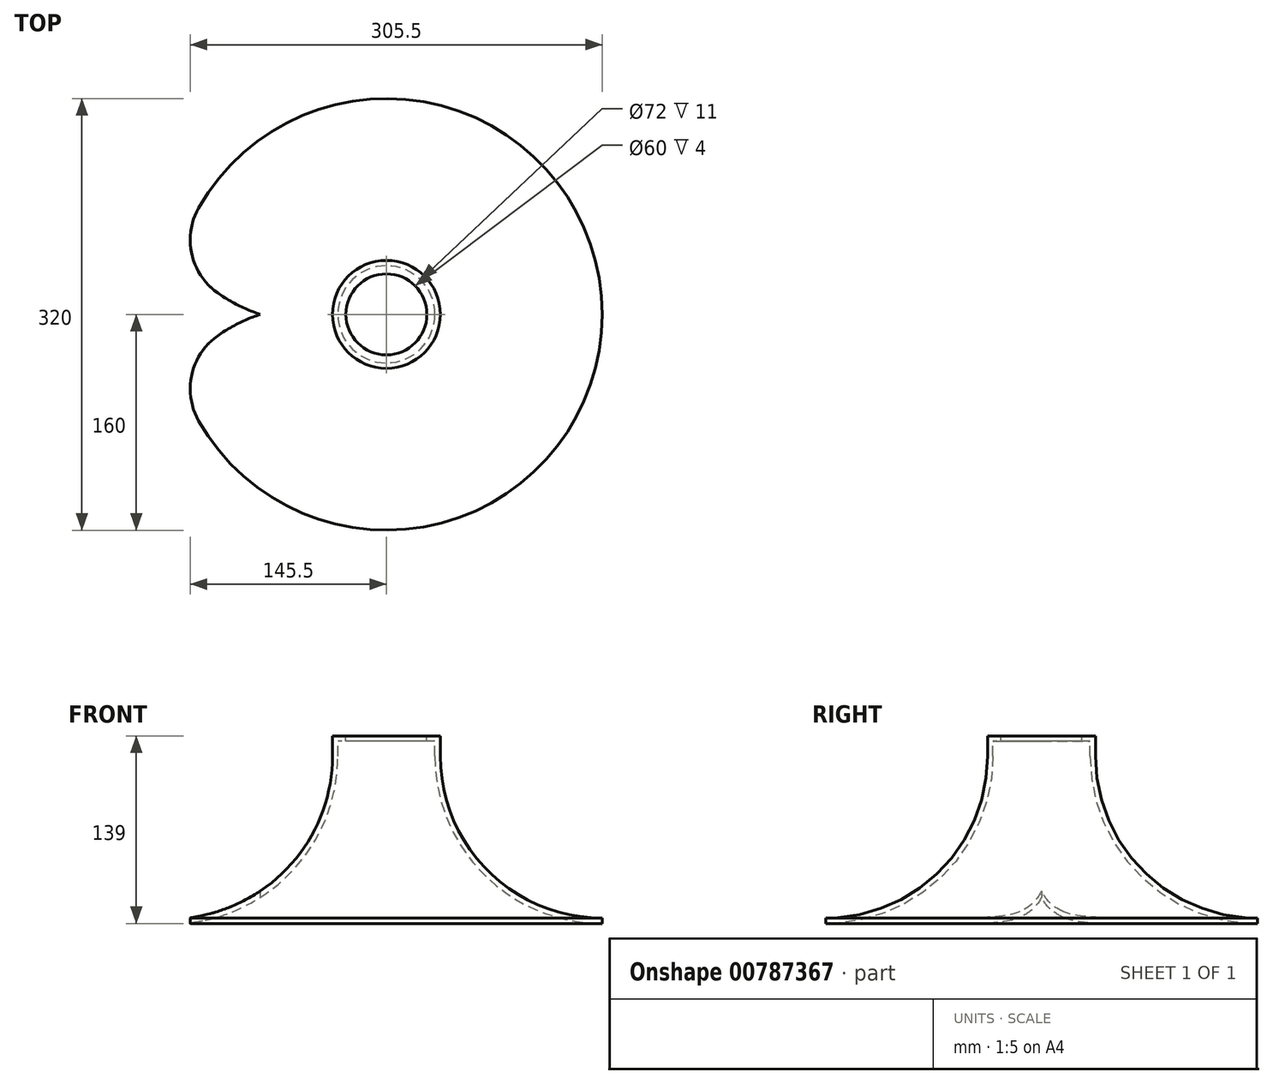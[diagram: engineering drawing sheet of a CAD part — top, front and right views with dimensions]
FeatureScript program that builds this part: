
annotation { "Feature Type Name" : "Feature", "Feature Type Description" : "" }
export const myFeature = defineFeature(function(context is Context, id is Id, definition is map)
    precondition{}
    {
        {
            var Q0;
            Q0=qCreatedBy(makeId("Front.planeOp"),FACE);
            var sketch = newSketch(context, id + "F0", { "sketchPlane" : qUnion([Q0])});
            skArc(sketch, "E0", {"start": v(0, -120) * mm, "mid": v(84.85, -84.85) * mm, "end": v(120, 0) * mm});
            skArc(sketch, "E1", {"start": v(0, -124) * mm, "mid": v(87.68, -87.68) * mm, "end": v(124, 0) * mm});
            skLineSegment(sketch, "E2", {"start": v(0, -124) * mm, "end": v(0, -120) * mm});
            skLineSegment(sketch, "E3.top", {"start": v(120, 15) * mm, "end": v(124, 15) * mm});
            skLineSegment(sketch, "E3.left", {"start": v(120, 0) * mm, "end": v(120, 15) * mm});
            skLineSegment(sketch, "E4.bottom", {"start": v(124, 15) * mm, "end": v(130, 15) * mm});
            skLineSegment(sketch, "E4.top", {"start": v(124, 11) * mm, "end": v(130, 11) * mm});
            skLineSegment(sketch, "E4.right", {"start": v(130, 15) * mm, "end": v(130, 11) * mm});
            skLineSegment(sketch, "E5", {"start": v(124, 11) * mm, "end": v(124, 0) * mm});
            skLineSegment(sketch, "E6", {"start": v(160, 28.66) * mm, "end": v(160, -153.48) * mm, "construction": true});
            skSolve(sketch);
        }
        {
            var Q0;
            Q0=makeQuery(id+"F0.imprint","IMPRINT",FACE,{"disambiguationData":[TD([[makeQuery(id+"F0.imprint","IMPRINT",EDGE,{"derivedFrom":sQuery(id+"F0.wireOp",EDGE,"E0")}),-1.0]])]});
            var Q1;
            Q1=sQuery(id+"F0.wireOp",EDGE,"E6");
            revolve(context, id + "F1", {"surfaceOperationType" : NewSurfaceOperationType.NEW, "entities" : qUnion([Q0]), "axis" : qUnion([Q1]), "revolveType" : RevolveType.FULL});
        }
        {
            var Q0;
            Q0=qCreatedBy(makeId("Top.planeOp"),FACE);
            cPlane(context, id + "F2", {"entities" : qUnion([Q0]), "cplaneType" : CPlaneType.OFFSET, "offset" : 140 * mm, "oppositeDirection" : true, "width" : 150 * mm, "height" : 150 * mm});
        }
        {
            var Q0;
            Q0=qCreatedBy(id+"F2.planeOp",FACE);
            var sketch = newSketch(context, id + "F3", { "sketchPlane" : qUnion([Q0])});
            skArc(sketch, "E7", {"start": v(0, 54.14) * mm, "mid": v(28.25, 20.93) * mm, "end": v(66.5, 0) * mm});
            skLineSegment(sketch, "E8", {"start": v(0, 54.14) * mm, "end": v(0, 0) * mm});
            skLineSegment(sketch, "E9", {"start": v(0, 0) * mm, "end": v(0, -54.14) * mm});
            skArc(sketch, "E10", {"start": v(66.5, 0) * mm, "mid": v(28.25, -20.93) * mm, "end": v(0, -54.14) * mm});
            skSolve(sketch);
        }
        {
            var Q0;
            Q0=makeQuery(id+"F3.imprint","IMPRINT",FACE,{"disambiguationData":[TD([[makeQuery(id+"F3.imprint","IMPRINT",EDGE,{"derivedFrom":sQuery(id+"F3.wireOp",EDGE,"E7")}),-1.0]])]});
            extrude(context, id + "F4", {"entities" : qUnion([Q0]), "operationType" : NewBodyOperationType.REMOVE, "depth" : 67 * mm, "offsetDistance" : 25 * mm});
        }
        {
            var Q0;
            Q0=makeQuery(id+"F4.boolean.opBoolean","INTERSECT",EDGE,{"derivedFrom":[makeQuery(id+"F1.opRevolve","SWEPT_FACE",FACE,{"disambiguationData":[OSD([sQuery(id+"F0.wireOp",EDGE,"E2")])]}),makeQuery(id+"F4.opExtrude","SWEPT_FACE",FACE,{"disambiguationData":[OSD([sQuery(id+"F3.wireOp",EDGE,"E10")])]})]});
            var Q1;
            Q1=makeQuery(id+"F4.boolean.opBoolean","INTERSECT",EDGE,{"derivedFrom":[makeQuery(id+"F1.opRevolve","SWEPT_FACE",FACE,{"disambiguationData":[OSD([sQuery(id+"F0.wireOp",EDGE,"E2")])]}),makeQuery(id+"F4.opExtrude","SWEPT_FACE",FACE,{"disambiguationData":[OSD([sQuery(id+"F3.wireOp",EDGE,"E7")])]})]});
            var Q2;
            {var subQ0=sQuery(id+"F3.wireOp",EDGE,"E10");var subQ2=makeQuery(id+"F4.boolean.opBoolean","COPY",FACE,{"derivedFrom":makeQuery(id+"F4.opExtrude","SWEPT_FACE",FACE,{"disambiguationData":[OSD([sQuery(id+"F3.wireOp",EDGE,"E7")])]})});Q2=makeQuery(id+"Fn1Wq9QeC9tYu7w_1.5.F4.boolean.opBoolean","INTERSECT",EDGE,{"derivedFrom":[makeQuery(id+"Fn1Wq9QeC9tYu7w_1.4.F4.boolean.opBoolean","SPLIT",FACE,{"disambiguationData":[TD([subQ2])],"derivedFrom":makeQuery(id+"Fn1Wq9QeC9tYu7w_1.3.F4.boolean.opBoolean","SPLIT",FACE,{"disambiguationData":[TD([subQ2])],"derivedFrom":makeQuery(id+"Fn1Wq9QeC9tYu7w_1.2.F4.boolean.opBoolean","SPLIT",FACE,{"disambiguationData":[TD([subQ2])],"derivedFrom":makeQuery(id+"Fn1Wq9QeC9tYu7w_1.1.F4.boolean.opBoolean","SPLIT",FACE,{"disambiguationData":[TD([subQ2])],"derivedFrom":makeQuery(id+"F1.opRevolve","SWEPT_FACE",FACE,{"disambiguationData":[OSD([sQuery(id+"F0.wireOp",EDGE,"E2")])]})})})})}),makeQuery(id+"Fn1Wq9QeC9tYu7w_1.5.F4.opExtrude","SWEPT_FACE",FACE,{"disambiguationData":[OSD([subQ0])]})]});}
            var Q3;
            {var subQ0=sQuery(id+"F3.wireOp",EDGE,"E7");var subQ2=makeQuery(id+"F4.boolean.opBoolean","COPY",FACE,{"derivedFrom":makeQuery(id+"F4.opExtrude","SWEPT_FACE",FACE,{"disambiguationData":[OSD([subQ0])]})});Q3=makeQuery(id+"Fn1Wq9QeC9tYu7w_1.5.F4.boolean.opBoolean","INTERSECT",EDGE,{"derivedFrom":[makeQuery(id+"Fn1Wq9QeC9tYu7w_1.4.F4.boolean.opBoolean","SPLIT",FACE,{"disambiguationData":[TD([subQ2])],"derivedFrom":makeQuery(id+"Fn1Wq9QeC9tYu7w_1.3.F4.boolean.opBoolean","SPLIT",FACE,{"disambiguationData":[TD([subQ2])],"derivedFrom":makeQuery(id+"Fn1Wq9QeC9tYu7w_1.2.F4.boolean.opBoolean","SPLIT",FACE,{"disambiguationData":[TD([subQ2])],"derivedFrom":makeQuery(id+"Fn1Wq9QeC9tYu7w_1.1.F4.boolean.opBoolean","SPLIT",FACE,{"disambiguationData":[TD([subQ2])],"derivedFrom":makeQuery(id+"F1.opRevolve","SWEPT_FACE",FACE,{"disambiguationData":[OSD([sQuery(id+"F0.wireOp",EDGE,"E2")])]})})})})}),makeQuery(id+"Fn1Wq9QeC9tYu7w_1.5.F4.opExtrude","SWEPT_FACE",FACE,{"disambiguationData":[OSD([subQ0])]})]});}
            var Q4;
            {var subQ0=sQuery(id+"F3.wireOp",EDGE,"E10");var subQ2=makeQuery(id+"F4.boolean.opBoolean","COPY",FACE,{"derivedFrom":makeQuery(id+"F4.opExtrude","SWEPT_FACE",FACE,{"disambiguationData":[OSD([sQuery(id+"F3.wireOp",EDGE,"E7")])]})});Q4=makeQuery(id+"Fn1Wq9QeC9tYu7w_1.4.F4.boolean.opBoolean","INTERSECT",EDGE,{"derivedFrom":[makeQuery(id+"Fn1Wq9QeC9tYu7w_1.3.F4.boolean.opBoolean","SPLIT",FACE,{"disambiguationData":[TD([subQ2])],"derivedFrom":makeQuery(id+"Fn1Wq9QeC9tYu7w_1.2.F4.boolean.opBoolean","SPLIT",FACE,{"disambiguationData":[TD([subQ2])],"derivedFrom":makeQuery(id+"Fn1Wq9QeC9tYu7w_1.1.F4.boolean.opBoolean","SPLIT",FACE,{"disambiguationData":[TD([subQ2])],"derivedFrom":makeQuery(id+"F1.opRevolve","SWEPT_FACE",FACE,{"disambiguationData":[OSD([sQuery(id+"F0.wireOp",EDGE,"E2")])]})})})}),makeQuery(id+"Fn1Wq9QeC9tYu7w_1.4.F4.opExtrude","SWEPT_FACE",FACE,{"disambiguationData":[OSD([subQ0])]})]});}
            var Q5;
            {var subQ0=sQuery(id+"F3.wireOp",EDGE,"E7");var subQ2=makeQuery(id+"F4.boolean.opBoolean","COPY",FACE,{"derivedFrom":makeQuery(id+"F4.opExtrude","SWEPT_FACE",FACE,{"disambiguationData":[OSD([subQ0])]})});Q5=makeQuery(id+"Fn1Wq9QeC9tYu7w_1.4.F4.boolean.opBoolean","INTERSECT",EDGE,{"derivedFrom":[makeQuery(id+"Fn1Wq9QeC9tYu7w_1.3.F4.boolean.opBoolean","SPLIT",FACE,{"disambiguationData":[TD([subQ2])],"derivedFrom":makeQuery(id+"Fn1Wq9QeC9tYu7w_1.2.F4.boolean.opBoolean","SPLIT",FACE,{"disambiguationData":[TD([subQ2])],"derivedFrom":makeQuery(id+"Fn1Wq9QeC9tYu7w_1.1.F4.boolean.opBoolean","SPLIT",FACE,{"disambiguationData":[TD([subQ2])],"derivedFrom":makeQuery(id+"F1.opRevolve","SWEPT_FACE",FACE,{"disambiguationData":[OSD([sQuery(id+"F0.wireOp",EDGE,"E2")])]})})})}),makeQuery(id+"Fn1Wq9QeC9tYu7w_1.4.F4.opExtrude","SWEPT_FACE",FACE,{"disambiguationData":[OSD([subQ0])]})]});}
            var Q6;
            {var subQ0=sQuery(id+"F3.wireOp",EDGE,"E10");var subQ2=makeQuery(id+"F4.boolean.opBoolean","COPY",FACE,{"derivedFrom":makeQuery(id+"F4.opExtrude","SWEPT_FACE",FACE,{"disambiguationData":[OSD([sQuery(id+"F3.wireOp",EDGE,"E7")])]})});Q6=makeQuery(id+"Fn1Wq9QeC9tYu7w_1.3.F4.boolean.opBoolean","INTERSECT",EDGE,{"derivedFrom":[makeQuery(id+"Fn1Wq9QeC9tYu7w_1.2.F4.boolean.opBoolean","SPLIT",FACE,{"disambiguationData":[TD([subQ2])],"derivedFrom":makeQuery(id+"Fn1Wq9QeC9tYu7w_1.1.F4.boolean.opBoolean","SPLIT",FACE,{"disambiguationData":[TD([subQ2])],"derivedFrom":makeQuery(id+"F1.opRevolve","SWEPT_FACE",FACE,{"disambiguationData":[OSD([sQuery(id+"F0.wireOp",EDGE,"E2")])]})})}),makeQuery(id+"Fn1Wq9QeC9tYu7w_1.3.F4.opExtrude","SWEPT_FACE",FACE,{"disambiguationData":[OSD([subQ0])]})]});}
            var Q7;
            {var subQ0=sQuery(id+"F3.wireOp",EDGE,"E7");var subQ2=makeQuery(id+"F4.boolean.opBoolean","COPY",FACE,{"derivedFrom":makeQuery(id+"F4.opExtrude","SWEPT_FACE",FACE,{"disambiguationData":[OSD([subQ0])]})});Q7=makeQuery(id+"Fn1Wq9QeC9tYu7w_1.3.F4.boolean.opBoolean","INTERSECT",EDGE,{"derivedFrom":[makeQuery(id+"Fn1Wq9QeC9tYu7w_1.2.F4.boolean.opBoolean","SPLIT",FACE,{"disambiguationData":[TD([subQ2])],"derivedFrom":makeQuery(id+"Fn1Wq9QeC9tYu7w_1.1.F4.boolean.opBoolean","SPLIT",FACE,{"disambiguationData":[TD([subQ2])],"derivedFrom":makeQuery(id+"F1.opRevolve","SWEPT_FACE",FACE,{"disambiguationData":[OSD([sQuery(id+"F0.wireOp",EDGE,"E2")])]})})}),makeQuery(id+"Fn1Wq9QeC9tYu7w_1.3.F4.opExtrude","SWEPT_FACE",FACE,{"disambiguationData":[OSD([subQ0])]})]});}
            var Q8;
            {var subQ0=sQuery(id+"F3.wireOp",EDGE,"E10");Q8=makeQuery(id+"Fn1Wq9QeC9tYu7w_1.2.F4.boolean.opBoolean","INTERSECT",EDGE,{"derivedFrom":[makeQuery(id+"Fn1Wq9QeC9tYu7w_1.1.F4.boolean.opBoolean","SPLIT",FACE,{"disambiguationData":[TD([makeQuery(id+"F4.boolean.opBoolean","COPY",FACE,{"derivedFrom":makeQuery(id+"F4.opExtrude","SWEPT_FACE",FACE,{"disambiguationData":[OSD([sQuery(id+"F3.wireOp",EDGE,"E7")])]})})])],"derivedFrom":makeQuery(id+"F1.opRevolve","SWEPT_FACE",FACE,{"disambiguationData":[OSD([sQuery(id+"F0.wireOp",EDGE,"E2")])]})}),makeQuery(id+"Fn1Wq9QeC9tYu7w_1.2.F4.opExtrude","SWEPT_FACE",FACE,{"disambiguationData":[OSD([subQ0])]})]});}
            var Q9;
            {var subQ0=sQuery(id+"F3.wireOp",EDGE,"E7");Q9=makeQuery(id+"Fn1Wq9QeC9tYu7w_1.2.F4.boolean.opBoolean","INTERSECT",EDGE,{"derivedFrom":[makeQuery(id+"Fn1Wq9QeC9tYu7w_1.1.F4.boolean.opBoolean","SPLIT",FACE,{"disambiguationData":[TD([makeQuery(id+"F4.boolean.opBoolean","COPY",FACE,{"derivedFrom":makeQuery(id+"F4.opExtrude","SWEPT_FACE",FACE,{"disambiguationData":[OSD([subQ0])]})})])],"derivedFrom":makeQuery(id+"F1.opRevolve","SWEPT_FACE",FACE,{"disambiguationData":[OSD([sQuery(id+"F0.wireOp",EDGE,"E2")])]})}),makeQuery(id+"Fn1Wq9QeC9tYu7w_1.2.F4.opExtrude","SWEPT_FACE",FACE,{"disambiguationData":[OSD([subQ0])]})]});}
            var Q10;
            Q10=makeQuery(id+"Fn1Wq9QeC9tYu7w_1.1.F4.boolean.opBoolean","INTERSECT",EDGE,{"derivedFrom":[makeQuery(id+"F1.opRevolve","SWEPT_FACE",FACE,{"disambiguationData":[OSD([sQuery(id+"F0.wireOp",EDGE,"E2")])]}),makeQuery(id+"Fn1Wq9QeC9tYu7w_1.1.F4.opExtrude","SWEPT_FACE",FACE,{"disambiguationData":[OSD([sQuery(id+"F3.wireOp",EDGE,"E10")])]})]});
            var Q11;
            Q11=makeQuery(id+"Fn1Wq9QeC9tYu7w_1.1.F4.boolean.opBoolean","INTERSECT",EDGE,{"derivedFrom":[makeQuery(id+"F1.opRevolve","SWEPT_FACE",FACE,{"disambiguationData":[OSD([sQuery(id+"F0.wireOp",EDGE,"E2")])]}),makeQuery(id+"Fn1Wq9QeC9tYu7w_1.1.F4.opExtrude","SWEPT_FACE",FACE,{"disambiguationData":[OSD([sQuery(id+"F3.wireOp",EDGE,"E7")])]})]});
            fillet(context, id + "F5", {"entities" : qUnion([Q0, Q1, Q2, Q3, Q4, Q5, Q6, Q7, Q8, Q9, Q10, Q11]), "radius" : 47.95 * mm, "tangentPropagation" : true, "allowEdgeOverflow" : false});
        }
    });
